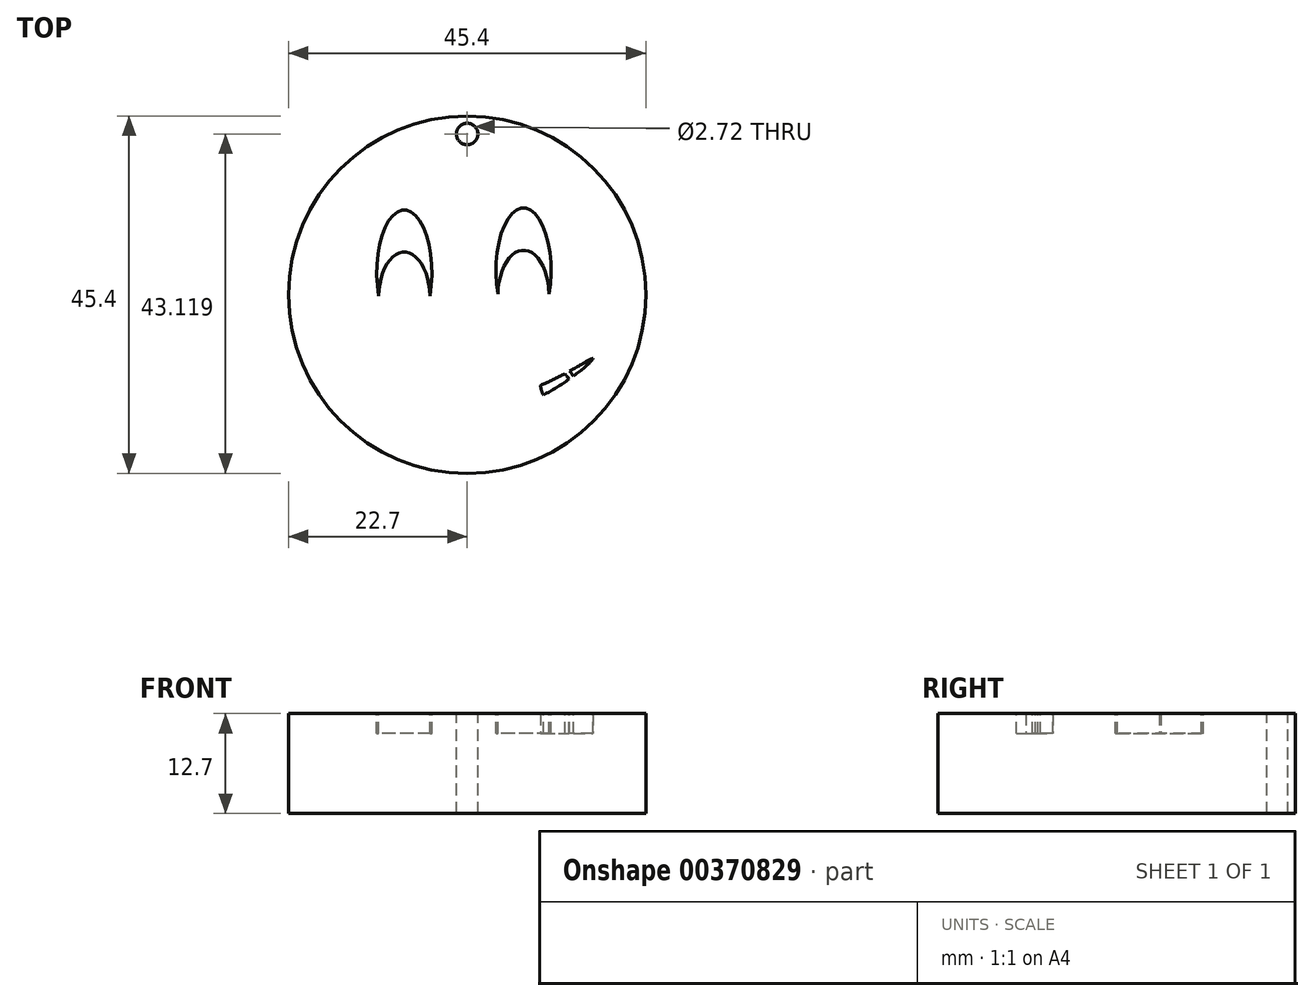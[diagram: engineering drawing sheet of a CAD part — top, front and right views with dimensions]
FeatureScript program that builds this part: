
annotation { "Feature Type Name" : "Feature", "Feature Type Description" : "" }
export const myFeature = defineFeature(function(context is Context, id is Id, definition is map)
    precondition{}
    {
        {
            var Q0;
            Q0=qCreatedBy(makeId("Top.planeOp"),FACE);
            var sketch = newSketch(context, id + "F0", { "sketchPlane" : qUnion([Q0])});
            skCircle(sketch, "E0", {"center": v(0, 0) * mm, "radius": 22.7 * mm});
            skSolve(sketch);
        }
        {
            var Q0;
            Q0=makeQuery(id+"F0.imprint","IMPRINT",FACE,{"disambiguationData":[TD([[makeQuery(id+"F0.imprint","IMPRINT",EDGE,{"derivedFrom":sQuery(id+"F0.wireOp",EDGE,"E0")}),1.0]])]});
            extrude(context, id + "F1", {"entities" : qUnion([Q0]), "depth" : 12.7 * mm});
        }
        {
            var Q0;
            Q0=makeQuery(id+"F1.opExtrude","CAP_FACE",FACE,{"disambiguationData":[OSD([sQuery(id+"F0.wireOp",EDGE,"E0")])],"isStart":false});
            var sketch = newSketch(context, id + "F2", { "sketchPlane" : qUnion([Q0])});
            skEllipticalArc(sketch, "E1", {});
            skEllipticalArc(sketch, "E2", {});
            skEllipticalArc(sketch, "E3", {});
            skEllipticalArc(sketch, "E4", {});
            skFitSpline(sketch, "E5", {"points": [v(-16.1, -8.29) * mm, v(-0.36, -15.68) * mm, v(16, -8.1) * mm, v(-0.36, -13.88) * mm, v(-16.1, -8.29) * mm]});
            skFitSpline(sketch, "E6", {"points": [v(16, -8.1) * mm, v(16.49, -15.6) * mm, v(9.33, -11.53) * mm, v(16, -8.1) * mm]});
            skEllipticalArc(sketch, "E7", {});
            const initialGuessF2  = {"E1": [0.0071570465693169575, 0.003074111602474311, 0, 1, 0.007933032233268023, 0.003504754738852713, 4.327223935529677, 1.9559613716499085], "E2": [0.0071570465693169575, -0.0001442612156082601, 0, -1, 0.005796437151730061, 0.003250721503016386, 1.6118393743180706, 4.671345932861516], "E3": [-0.00798518002748612, 0.002836274944016495, 0, 1, 0.007933032233268023, 0.003504754738852713, 4.327223935529677, 1.9559613716499085], "E4": [-0.00798518002748612, -0.0003820978740660761, 0, -1, 0.005796437151730061, 0.003250721503016386, 1.6118393743180706, 4.671345932861516], "E7": [0.012722297295366452, -0.009857580734337448, 0.5978106483397688, -0.8016373424009047, 0.004234819493438222, 0.0003414077873771633, 4.700394494684409, 1.5593019218451307]};
            skSetInitialGuess(sketch, initialGuessF2);
            skSolve(sketch);
        }
        {
            var Q0;
            {var subQ0=sQuery(id+"F2.wireOp",EDGE,"E6");var subQ1=sQuery(id+"F2.wireOp",EDGE,"E5");var subQ2=makeQuery(id+"F2.imprint","INTERSECT",VERTEX,{"disambiguationData":[OD(0.0)],"derivedFrom":[subQ1,subQ0]});Q0=makeQuery(id+"F2.imprint","IMPRINT",FACE,{"disambiguationData":[TD([[makeQuery(id+"F2.imprint","IMPRINT",EDGE,{"disambiguationData":[TD([[subQ2,-1.0]])],"derivedFrom":subQ1}),1.0]])]});}
            var Q1;
            {var subQ0=sQuery(id+"F2.wireOp",EDGE,"E6");var subQ1=sQuery(id+"F2.wireOp",EDGE,"E5");var subQ2=makeQuery(id+"F2.imprint","INTERSECT",VERTEX,{"disambiguationData":[OD(1.0)],"derivedFrom":[subQ1,subQ0]});Q1=makeQuery(id+"F2.imprint","IMPRINT",FACE,{"disambiguationData":[TD([[makeQuery(id+"F2.imprint","IMPRINT",EDGE,{"disambiguationData":[TD([[subQ2,1.0]])],"derivedFrom":subQ1}),1.0]])]});}
            var Q2;
            Q2=makeQuery(id+"F2.imprint","IMPRINT",FACE,{"disambiguationData":[TD([[makeQuery(id+"F2.imprint","IMPRINT",EDGE,{"derivedFrom":sQuery(id+"F2.wireOp",EDGE,"E3")}),1.0]])]});
            var Q3;
            Q3=makeQuery(id+"F2.imprint","IMPRINT",FACE,{"disambiguationData":[TD([[makeQuery(id+"F2.imprint","IMPRINT",EDGE,{"derivedFrom":sQuery(id+"F2.wireOp",EDGE,"E1")}),1.0]])]});
            var Q4;
            {var subQ7=sQuery(id+"F2.wireOp",EDGE,"E7");Q4=makeQuery(id+"F2.imprint","IMPRINT",FACE,{"disambiguationData":[TD([[makeQuery(id+"F2.imprint","IMPRINT",EDGE,{"derivedFrom":subQ7}),-1.0]])]});}
            extrude(context, id + "F3", {"entities" : qUnion([Q0, Q1, Q2, Q3, Q4]), "operationType" : NewBodyOperationType.REMOVE, "oppositeDirection" : true, "depth" : 2.54 * mm});
        }
        {
            var Q0;
            Q0=makeQuery(id+"F1.opExtrude","CAP_FACE",FACE,{"disambiguationData":[OSD([sQuery(id+"F0.wireOp",EDGE,"E0")])],"isStart":false});
            var sketch = newSketch(context, id + "F4", { "sketchPlane" : qUnion([Q0])});
            skCircle(sketch, "E8", {"center": v(0, 20.42) * mm, "radius": 1.36 * mm});
            skSolve(sketch);
        }
        {
            var Q0;
            Q0=makeQuery(id+"F4.imprint","IMPRINT",FACE,{"disambiguationData":[TD([[makeQuery(id+"F4.imprint","IMPRINT",EDGE,{"derivedFrom":sQuery(id+"F4.wireOp",EDGE,"E8")}),1.0]])]});
            extrude(context, id + "F5", {"entities" : qUnion([Q0]), "operationType" : NewBodyOperationType.REMOVE, "oppositeDirection" : true, "depth" : 12.7 * mm});
        }
    });
